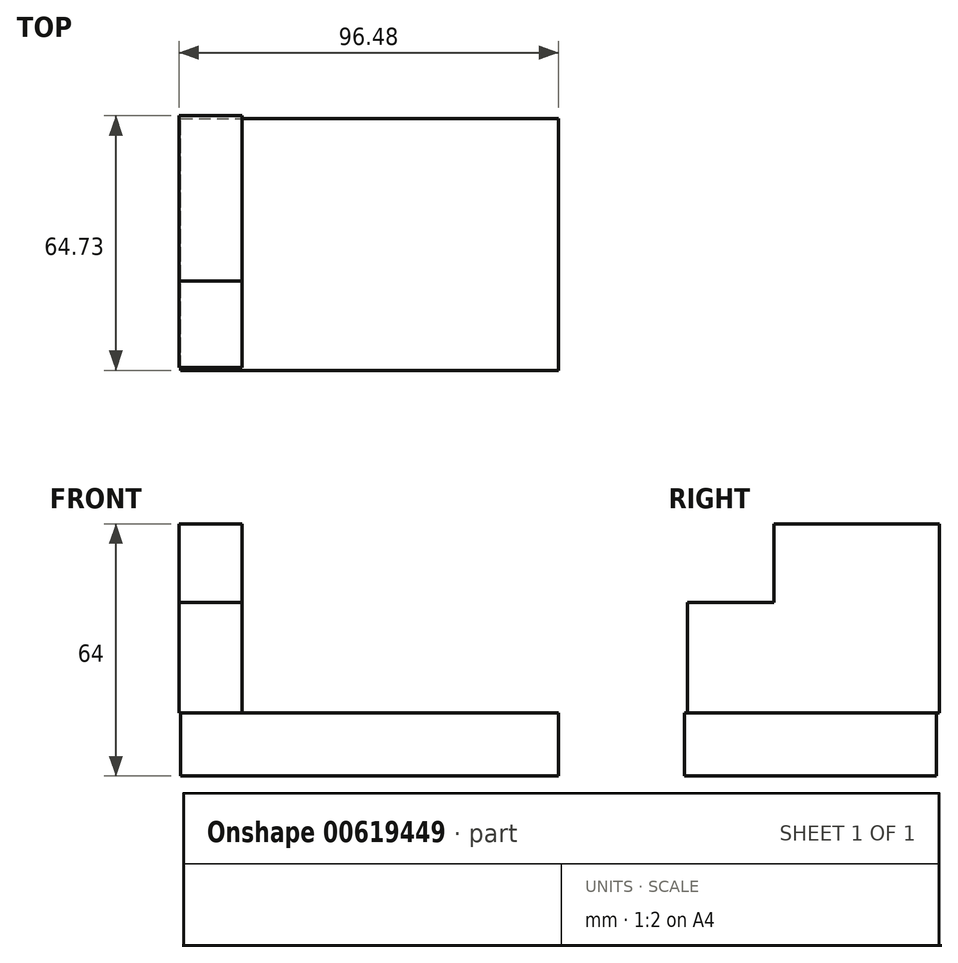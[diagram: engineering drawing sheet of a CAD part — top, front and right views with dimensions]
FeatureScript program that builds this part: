
annotation { "Feature Type Name" : "Feature", "Feature Type Description" : "" }
export const myFeature = defineFeature(function(context is Context, id is Id, definition is map)
    precondition{}
    {
        {
            var Q0;
            Q0=qCreatedBy(makeId("Top.planeOp"),FACE);
            var sketch = newSketch(context, id + "F0", { "sketchPlane" : qUnion([Q0])});
            skLineSegment(sketch, "E0.bottom", {"start": v(-53.1, -30.92) * mm, "end": v(42.9, -30.92) * mm});
            skLineSegment(sketch, "E0.top", {"start": v(-53.1, 33.08) * mm, "end": v(42.9, 33.08) * mm});
            skLineSegment(sketch, "E0.left", {"start": v(-53.1, -30.92) * mm, "end": v(-53.1, 33.08) * mm});
            skLineSegment(sketch, "E0.right", {"start": v(42.9, -30.92) * mm, "end": v(42.9, 33.08) * mm});
            skSolve(sketch);
        }
        {
            var Q0;
            Q0 = qSketchRegion(id + "F0", true);
            extrude(context, id + "F1", {"entities" : qUnion([Q0]), "depth" : 16 * mm, "offsetDistance" : 25.4 * mm});
        }
        {
            var Q0;
            Q0=makeQuery(id+"F1.opExtrude","CAP_FACE",FACE,{"disambiguationData":[OSD([sQuery(id+"F0.wireOp",EDGE,"E0.bottom"),sQuery(id+"F0.wireOp",EDGE,"E0.top"),sQuery(id+"F0.wireOp",EDGE,"E0.left"),sQuery(id+"F0.wireOp",EDGE,"E0.right")])],"isStart":false});
            var sketch = newSketch(context, id + "F2", { "sketchPlane" : qUnion([Q0])});
            skSolve(sketch);
        }
        {
            var Q0;
            Q0=makeQuery(id+"F2.imprint","IMPRINT",FACE,{"disambiguationData":[TD([[makeQuery(id+"F2.imprint","IMPRINT",EDGE,{"derivedFrom":makeQuery(id+"F1.opExtrude","CAP_EDGE",EDGE,{"disambiguationData":[OSD([sQuery(id+"F0.wireOp",EDGE,"E0.bottom")])],"isStart":false})}),1.0]])]});
            var sketch = newSketch(context, id + "F3", { "sketchPlane" : qUnion([Q0])});
            skLineSegment(sketch, "E1.bottom", {"start": v(-53.57, -30.19) * mm, "end": v(-37.57, -30.19) * mm});
            skLineSegment(sketch, "E1.top", {"start": v(-53.57, 33.81) * mm, "end": v(-37.57, 33.81) * mm});
            skLineSegment(sketch, "E1.left", {"start": v(-53.57, -30.19) * mm, "end": v(-53.57, 33.81) * mm});
            skLineSegment(sketch, "E1.right", {"start": v(-37.57, -30.19) * mm, "end": v(-37.57, 33.81) * mm});
            skSolve(sketch);
        }
        {
            var Q0;
            Q0 = qSketchRegion(id + "F3", true);
            extrude(context, id + "F4", {"entities" : qUnion([Q0]), "operationType" : NewBodyOperationType.ADD, "depth" : 28 * mm, "offsetDistance" : 25.4 * mm});
        }
        {
            var Q0;
            Q0=makeQuery(id+"F4.opExtrude","CAP_FACE",FACE,{"disambiguationData":[OSD([sQuery(id+"F3.wireOp",EDGE,"E1.bottom"),sQuery(id+"F3.wireOp",EDGE,"E1.top"),sQuery(id+"F3.wireOp",EDGE,"E1.left"),sQuery(id+"F3.wireOp",EDGE,"E1.right")])],"isStart":false});
            var sketch = newSketch(context, id + "F5", { "sketchPlane" : qUnion([Q0])});
            skLineSegment(sketch, "E2.bottom", {"start": v(-53.57, 33.81) * mm, "end": v(-37.57, 33.81) * mm});
            skLineSegment(sketch, "E2.top", {"start": v(-53.57, -8.19) * mm, "end": v(-37.57, -8.19) * mm});
            skLineSegment(sketch, "E2.left", {"start": v(-53.57, 33.81) * mm, "end": v(-53.57, -8.19) * mm});
            skLineSegment(sketch, "E2.right", {"start": v(-37.57, 33.81) * mm, "end": v(-37.57, -8.19) * mm});
            skSolve(sketch);
        }
        {
            var Q0;
            Q0 = qSketchRegion(id + "F5", true);
            extrude(context, id + "F6", {"entities" : qUnion([Q0]), "operationType" : NewBodyOperationType.ADD, "depth" : 20 * mm, "offsetDistance" : 25.4 * mm});
        }
    });
